# Revit family: LVRJ45
name_source: partatom
category: Communication Devices
revit_build: Autodesk Revit 2014 (Build: 20130308_1515(x64)
units: mm (PartAtom-declared; Revit-internal decimal feet)

## types (2) — shared parameters
Assembly Code = D5090
Black = Paint - Hubbell - Carbon Black
Default Elevation = 48 "
Description = Our Cat5e/6 enabled Low Voltage Switches are designed primarily
for applications where flying leads are not desired in the field. The
soft contours of this aesthetically pleasing design fits easily into
any decor. This switch is only available as a momentary version and
is suitable for use with PowerHUBB, NX, CX and even the Hubbell
Control Solutions (HCS) power packs so long as the connections to
the category cable are terminated per instructions and the pin-out
guidelines set by HCS.
Features = Attractive, architecturally pleasing design
• Momentary button action
• 2 and 3 buttons with Pilot Light
• Mounts to standard single-gang box
• Use standard decorator wall plates (order separately)
• Connect using Cat5e/6 cables
• Low voltage device: 24 VDC
• Five-year limited warranty
Height = 18.26 "
Manufacturer = Hubbell Control Solutions
Model = Low Voltage Switch RJ45 Enabled
Product Documentation Link = https://hubbellcdn.com
Product Page URL = https://www.hubbell.com
Type Comments = Low Voltage Switch Station
URL = https://www.hubbell.com
Warranty = 5-Years Warranty
White = Paint - Hubbell - Matte White
Width = 14.5 "

## per-type parameters (varying)
| type | 2 Switch Station | 3 Switch Station |
| LVSRJ45-2 Switch Station | Yes | No |
| LVSRJ45-3 Switch Station | No | Yes |

## geometry (parser evidence)
native form markers: Sweep x1
no freeform markers — native parametric forms only
